# Revit family: 80HS0106 OPEN
name_source: partatom
category: Specialty Equipment
units: mm (PartAtom-declared; Revit-internal decimal feet)

## family parameters
Always vertical = Yes
Cut with Voids When Loaded = No
Host = Wall
Part Type = Normal
Room Calculation Point = No
Round Connector Dimension = Use Diameter
Shared = No

## types (1)
- 80HS0106 OPEN
    Configuration = Open
    Description = Powder Coated Cold Rolled Steel, Stainless Steel and ABS
    Elevation = 13.38
    Frame Finish = Stainless Steel Finish
    Height = 13.38 "
    Manufacturer = The Sova Company
    Material(s) = Powder Coated Cold Rolled Steel, Stainless Steel and ABS
    Model = 80HS0106 OPEN
    Panel Finish = Stainless Steel Finish
    Product Site = https://choosesova.com
    Product Weight = 400lb
    SKU = 300-EHLD
    Shipping Height = 17.75 "
    Shipping Length = 80.75 "
    Shipping Width = 47.75 "
    URL = https://choosesova.com
    Unit Depth = 36.13 "
    Unit Height = 69 "
    Unit Length = 70.25 "
    Weight Capacity = 500lb

## geometry (parser evidence)
native form markers: Sweep x6
no freeform markers — native parametric forms only
